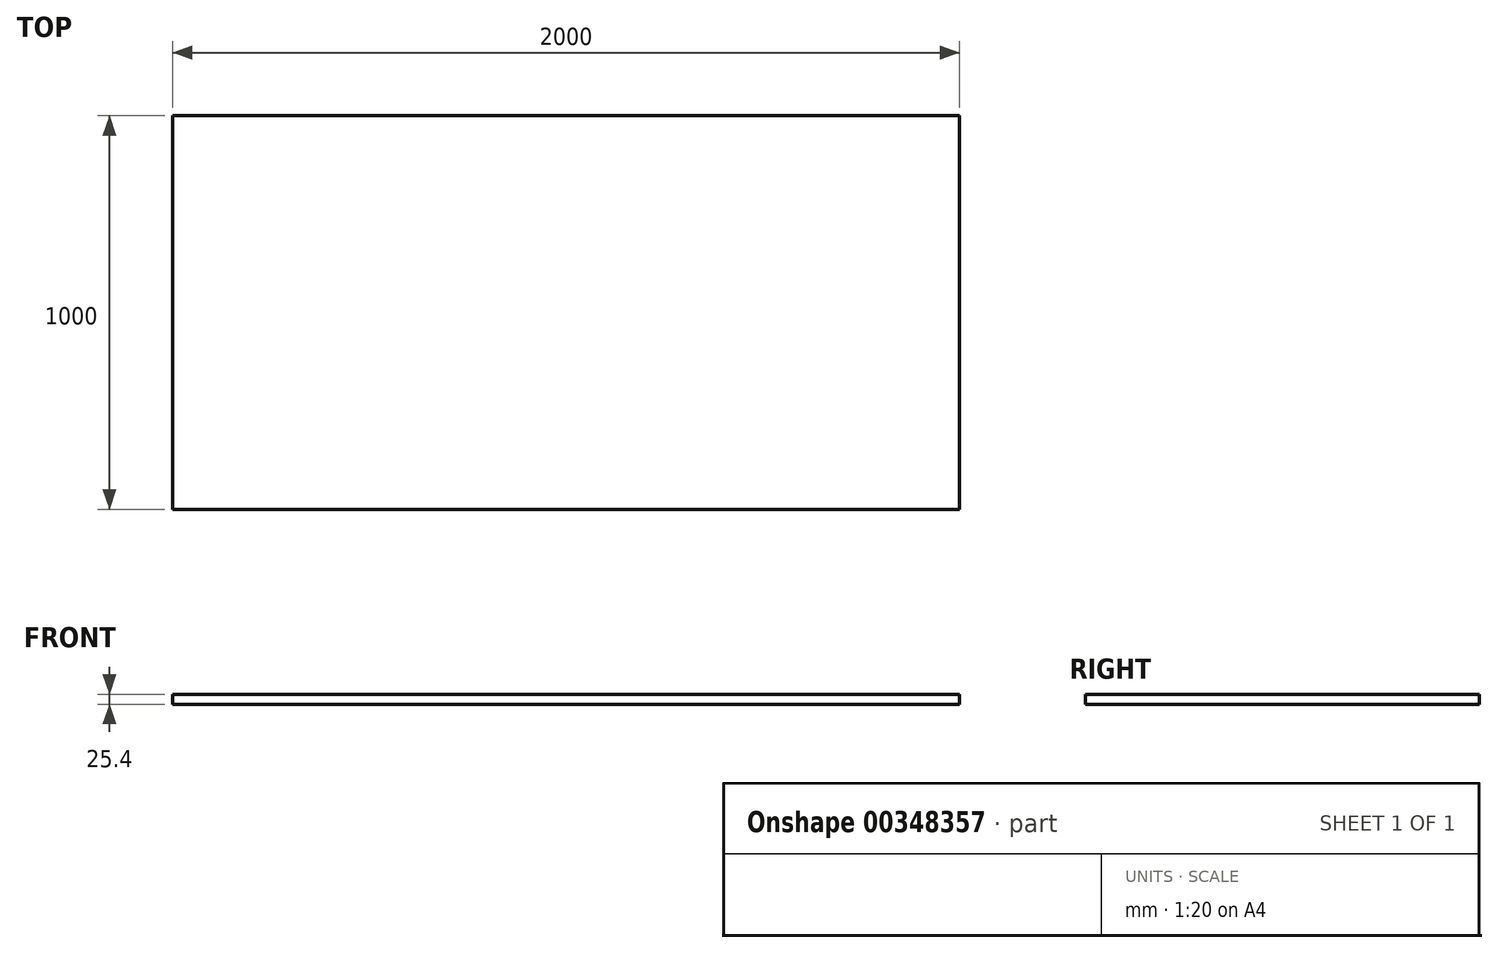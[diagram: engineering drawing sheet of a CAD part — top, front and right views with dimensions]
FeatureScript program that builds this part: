
annotation { "Feature Type Name" : "Feature", "Feature Type Description" : "" }
export const myFeature = defineFeature(function(context is Context, id is Id, definition is map)
    precondition{}
    {
        {
            var Q0;
            Q0=qCreatedBy(makeId("Top.planeOp"),FACE);
            var sketch = newSketch(context, id + "F0", { "sketchPlane" : qUnion([Q0])});
            skLineSegment(sketch, "E0.bottom", {"start": v(-1000, 500) * mm, "end": v(1000, 500) * mm});
            skLineSegment(sketch, "E0.top", {"start": v(-1000, -500) * mm, "end": v(1000, -500) * mm});
            skLineSegment(sketch, "E0.left", {"start": v(-1000, 500) * mm, "end": v(-1000, -500) * mm});
            skLineSegment(sketch, "E0.right", {"start": v(1000, 500) * mm, "end": v(1000, -500) * mm});
            skPoint(sketch, "E0.middle", {"position": v(0, 0) * mm});
            skSolve(sketch);
        }
        {
            var Q0;
            Q0=makeQuery(id+"F0.imprint","IMPRINT",FACE,{"disambiguationData":[TD([[makeQuery(id+"F0.imprint","IMPRINT",EDGE,{"derivedFrom":sQuery(id+"F0.wireOp",EDGE,"E0.bottom")}),-1.0]])]});
            extrude(context, id + "F1", {"entities" : qUnion([Q0]), "depth" : 25.4 * mm});
        }
    });
